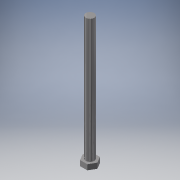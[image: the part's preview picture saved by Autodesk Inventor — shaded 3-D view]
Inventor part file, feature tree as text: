
AUTODESK INVENTOR PART (.ipt)
format: ipt  version: 2016 (Build 200138000, 138)  size: 118,272 bytes
history: native  units: in
note: dims shown in document units (in); Inventor stores cm internally (conversion verified against a paired STEP export)
features: extrude x2, sketch x2
ambient origin geometry x8: Origin, YZ Plane, XZ Plane, XY Plane, X Axis, Y Axis, Z Axis, Center Point
bodies: Solid1 (feature_tree)
feature tree (4):
  extrude  "Extrusion1"  Depth=0.2344in TaperAngle=0.0deg
  extrude  "Extrusion2"  Depth=5.5in TaperAngle=0.0deg
  sketch  "Sketch1"  dims[d0=0.5625in d1=0.2344in d2=0.0in]
  sketch  "Sketch2"  dims[d3=0.375in d4=5.5in d5=0.0in]
